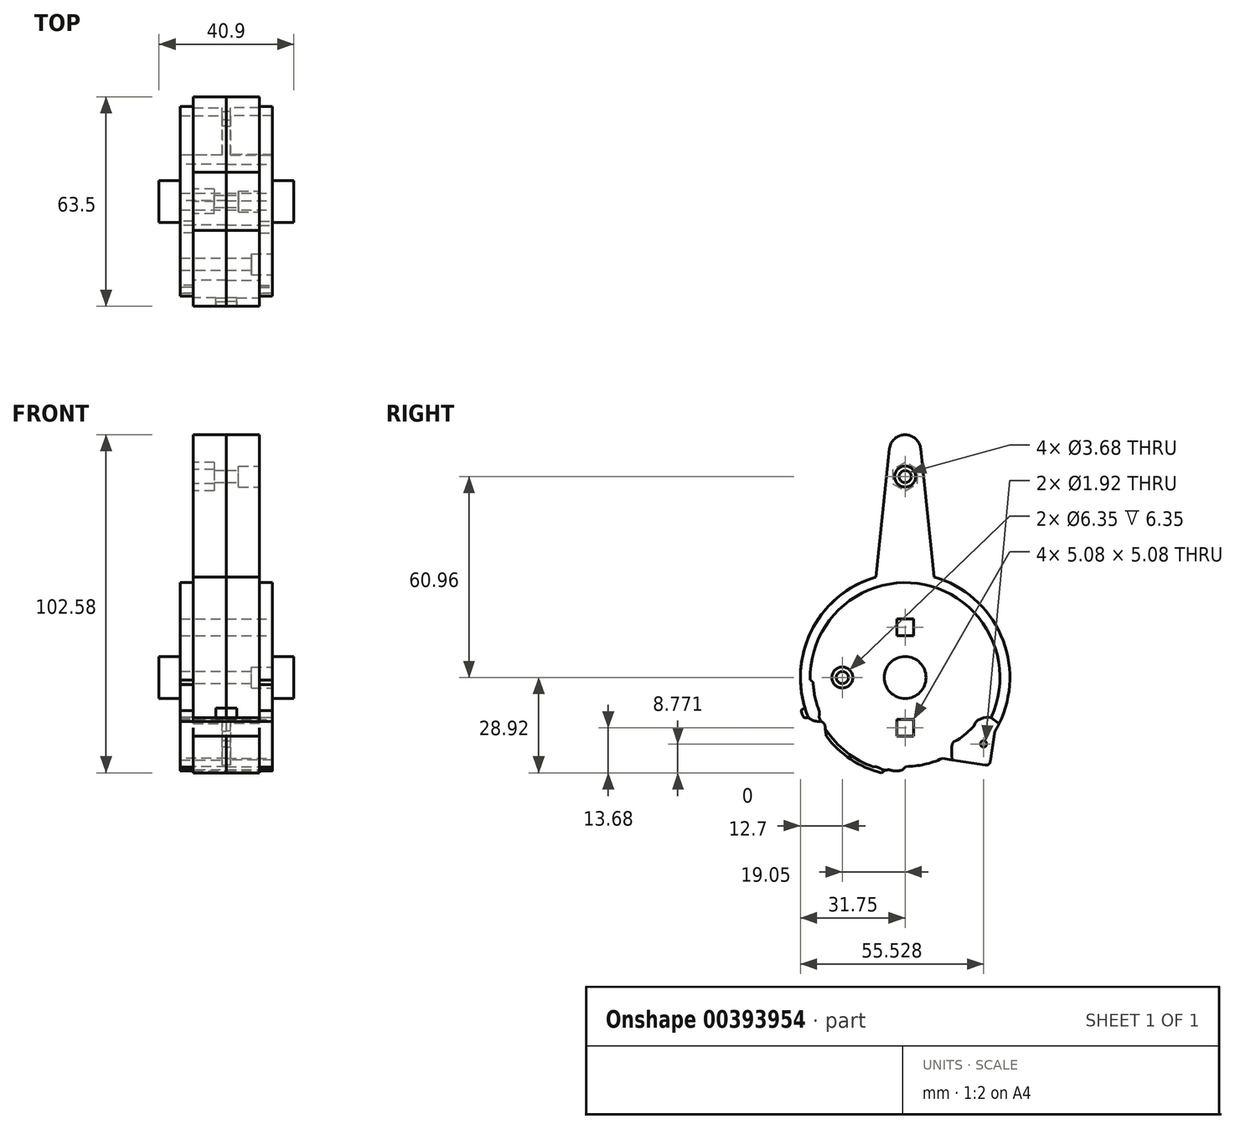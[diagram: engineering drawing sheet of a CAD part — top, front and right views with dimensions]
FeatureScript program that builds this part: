
annotation { "Feature Type Name" : "Feature", "Feature Type Description" : "" }
export const myFeature = defineFeature(function(context is Context, id is Id, definition is map)
    precondition{}
    {
        {
            var Q0;
            Q0=qCreatedBy(makeId("Right.planeOp"),FACE);
            var sketch = newSketch(context, id + "F0", { "sketchPlane" : qUnion([Q0])});
            skArc(sketch, "E0", {"start": v(-8.82, 30.5) * mm, "mid": v(-28.52, -13.96) * mm, "end": v(18.67, -25.68) * mm});
            skLineSegment(sketch, "E1", {"start": v(-4.74, 69.4) * mm, "end": v(-8.82, 30.5) * mm});
            skLineSegment(sketch, "E2", {"start": v(4.74, 69.4) * mm, "end": v(8.82, 30.5) * mm});
            skLineSegment(sketch, "E3", {"start": v(8.82, 30.5) * mm, "end": v(8.82, 30.5) * mm});
            skArc(sketch, "E4.filletArc", {"start": v(4.74, 69.4) * mm, "mid": v(0, 73.66) * mm, "end": v(-4.74, 69.4) * mm});
            skLineSegment(sketch, "E5", {"start": v(18.67, -25.68) * mm, "end": v(25.61, -26.77) * mm});
            skLineSegment(sketch, "E6", {"start": v(25.61, -26.77) * mm, "end": v(27.25, -16.29) * mm});
            skArc(sketch, "E7.trimOffspring", {"start": v(27.25, -16.29) * mm, "mid": v(29.54, 11.64) * mm, "end": v(8.82, 30.5) * mm});
            skSolve(sketch);
        }
        {
            var Q0;
            Q0=makeQuery(id+"F0.imprint","IMPRINT",FACE,{"disambiguationData":[TD([[makeQuery(id+"F0.imprint","IMPRINT",EDGE,{"derivedFrom":sQuery(id+"F0.wireOp",EDGE,"E0")}),1.0]])]});
            extrude(context, id + "F1", {"entities" : qUnion([Q0]), "depth" : 10.03 * mm});
        }
        {
            var Q0;
            Q0=qCreatedBy(makeId("Right.planeOp"),FACE);
            var sketch = newSketch(context, id + "F2", { "sketchPlane" : qUnion([Q0])});
            skCircle(sketch, "E8", {"center": v(0, 0) * mm, "radius": 28.77 * mm});
            skSolve(sketch);
        }
        {
            var Q0;
            Q0 = qSketchRegion(id + "F2", true);
            extrude(context, id + "F3", {"entities" : qUnion([Q0]), "operationType" : NewBodyOperationType.ADD, "depth" : 13.97 * mm});
        }
        {
            var Q0;
            Q0=qCreatedBy(makeId("Right.planeOp"),FACE);
            var sketch = newSketch(context, id + "F4", { "sketchPlane" : qUnion([Q0])});
            skCircle(sketch, "E9", {"center": v(0, 0) * mm, "radius": 6.35 * mm});
            skSolve(sketch);
        }
        {
            var Q0;
            Q0 = qSketchRegion(id + "F4", true);
            extrude(context, id + "F5", {"entities" : qUnion([Q0]), "operationType" : NewBodyOperationType.ADD, "depth" : 20.45 * mm});
        }
        {
            var Q0;
            Q0=makeQuery(id+"F3.opExtrude","CAP_FACE",FACE,{"disambiguationData":[OSD([sQuery(id+"F2.wireOp",EDGE,"E8")])],"isStart":false});
            var sketch = newSketch(context, id + "F6", { "sketchPlane" : qUnion([Q0])});
            skLineSegment(sketch, "E10.0", {"start": v(-8.82, 30.5) * mm, "end": v(-8.82, 30.5) * mm});
            skArc(sketch, "E11", {"start": v(-7.15, -28.92) * mm, "mid": v(-16.5, -24.81) * mm, "end": v(-23.9, -17.8) * mm});
            skFitSpline(sketch, "E12", {"points": [v(-7.15, -28.92) * mm, v(-6.46, -28.47) * mm, v(-6.2, -28.23) * mm, v(-5.89, -28.08) * mm, v(-5.55, -28.03) * mm, v(-5, -28) * mm, v(-4.31, -28.13) * mm, v(-3.35, -28.29) * mm, v(-2.28, -28.29) * mm, v(-1.37, -28.2) * mm, v(-0.54, -27.74) * mm, v(0.18, -27) * mm], "startDerivative": vector(7.94, 4.82) * mm, "endDerivative": vector(3.82, 6.45) * mm});
            skArc(sketch, "E13", {"start": v(0.18, -27) * mm, "mid": v(5.87, -26.35) * mm, "end": v(11.29, -24.53) * mm});
            skArc(sketch, "E14", {"start": v(-29.29, -12.26) * mm, "mid": v(-8.56, -30.57) * mm, "end": v(18.67, -25.68) * mm});
            skFitSpline(sketch, "E15", {"points": [v(-29.29, -12.26) * mm, v(-28.7, -12.62) * mm, v(-28.12, -12.97) * mm, v(-27.44, -13.17) * mm, v(-26.86, -13.25) * mm, v(-26.06, -13.36) * mm, v(-25.83, -13.34) * mm, v(-25.47, -13.37) * mm, v(-25.09, -13.51) * mm, v(-24.75, -13.83) * mm, v(-24.45, -14.2) * mm, v(-24.33, -14.51) * mm, v(-24.28, -14.82) * mm, v(-24.27, -15.1) * mm, v(-24.22, -15.52) * mm, v(-24.15, -16.14) * mm, v(-23.9, -17.8) * mm], "startDerivative": vector(8.22, -5.06) * mm, "endDerivative": vector(3.58, -22.61) * mm});
            skLineSegment(sketch, "E16.0", {"start": v(11.29, -24.53) * mm, "end": v(18.67, -25.68) * mm});
            skPoint(sketch, "E17.orphan", {"position": v(18.67, -25.68) * mm});
            skPoint(sketch, "E18.orphan", {"position": v(25.61, -26.77) * mm});
            skSolve(sketch);
        }
        {
            var Q0;
            Q0 = qSketchRegion(id + "F6", true);
            extrude(context, id + "F7", {"entities" : qUnion([Q0]), "operationType" : NewBodyOperationType.REMOVE, "endBound" : BoundingType.THROUGH_ALL, "oppositeDirection" : true, "depth" : 25.4 * mm});
        }
        {
            var Q0;
            Q0=qCreatedBy(makeId("Right.planeOp"),FACE);
            var sketch = newSketch(context, id + "F8", { "sketchPlane" : qUnion([Q0])});
            skFitSpline(sketch, "E19", {"points": [v(-29.98, -9.37) * mm, v(-30.97, -9.54) * mm, v(-31.46, -9.91) * mm, v(-31.42, -10.4) * mm, v(-31.3, -11) * mm, v(-31.05, -11.53) * mm, v(-30.78, -12.05) * mm, v(-30.13, -12.26) * mm, v(-29.34, -12.26) * mm, v(-29.1, -12.19) * mm, v(-29.98, -9.37) * mm]});
            skSolve(sketch);
        }
        {
            var Q0;
            Q0 = qSketchRegion(id + "F8", true);
            extrude(context, id + "F9", {"entities" : qUnion([Q0]), "operationType" : NewBodyOperationType.ADD, "depth" : 3.17 * mm});
        }
        {
            var Q0;
            Q0=qCreatedBy(makeId("Right.planeOp"),FACE);
            cPlane(context, id + "F10", {"entities" : qUnion([Q0]), "cplaneType" : CPlaneType.OFFSET, "offset" : 1.27 * mm, "width" : 152.4 * mm, "height" : 152.4 * mm});
        }
        {
            var Q0;
            Q0=qCreatedBy(id+"F10.planeOp",FACE);
            var sketch = newSketch(context, id + "F11", { "sketchPlane" : qUnion([Q0])});
            skPoint(sketch, "E20.0", {"position": v(19.93, -25.88) * mm});
            skLineSegment(sketch, "E21.0", {"start": v(25.61, -26.77) * mm, "end": v(27.25, -16.29) * mm});
            skArc(sketch, "E22.0", {"start": v(27.25, -16.29) * mm, "mid": v(27.89, -15.17) * mm, "end": v(28.48, -14.03) * mm});
            skLineSegment(sketch, "E23", {"start": v(26.08, -12.14) * mm, "end": v(28.48, -14.03) * mm});
            skPoint(sketch, "E24.orphan", {"position": v(-25.47, -13.37) * mm});
            skPoint(sketch, "E25.orphan", {"position": v(8.82, 30.5) * mm});
            skLineSegment(sketch, "E26", {"start": v(14.25, -24.99) * mm, "end": v(25.61, -26.77) * mm});
            skFitSpline(sketch, "E27", {"points": [v(26.08, -12.14) * mm, v(24.03, -12.14) * mm, v(21.51, -13.45) * mm, v(20.75, -14.85) * mm, v(19.28, -16.22) * mm, v(17.23, -18.05) * mm, v(15.6, -19.12) * mm, v(14.47, -19.84) * mm, v(14.25, -24.99) * mm], "startDerivative": vector(-16.47, 2.03) * mm, "endDerivative": vector(2.36, -34.88) * mm});
            skSolve(sketch);
        }
        {
            var Q0;
            Q0 = qSketchRegion(id + "F11", true);
            extrude(context, id + "F12", {"entities" : qUnion([Q0]), "operationType" : NewBodyOperationType.REMOVE, "endBound" : BoundingType.THROUGH_ALL, "depth" : 25.4 * mm});
        }
        {
            var Q0;
            Q0=makeQuery(id+"F12.boolean.opBoolean","COPY",FACE,{"derivedFrom":makeQuery(id+"F12.opExtrude","CAP_FACE",FACE,{"disambiguationData":[OSD([sQuery(id+"F11.wireOp",EDGE,"8e69ba01-a64c-4ecc-a6ff-eef0bb5ade50.0"),sQuery(id+"F11.wireOp",EDGE,"E21.0"),sQuery(id+"F11.wireOp",EDGE,"E22.0"),sQuery(id+"F11.wireOp",EDGE,"E23"),sQuery(id+"F11.wireOp",EDGE,"E26")])],"isStart":true})});
            var sketch = newSketch(context, id + "F13", { "sketchPlane" : qUnion([Q0])});
            skCircle(sketch, "E28", {"center": v(23.78, -20.15) * mm, "radius": 0.96 * mm});
            skSolve(sketch);
        }
        {
            var Q0;
            Q0 = qSketchRegion(id + "F13", true);
            extrude(context, id + "F14", {"entities" : qUnion([Q0]), "operationType" : NewBodyOperationType.REMOVE, "endBound" : BoundingType.THROUGH_ALL, "oppositeDirection" : true, "depth" : 25.4 * mm});
        }
        {
            var Q0;
            {var subQ0=makeQuery(id+"F1.opExtrude","SWEPT_EDGE",EDGE,{"disambiguationData":[OSD([sQuery(id+"F0.wireOp",EDGE,"E5"),sQuery(id+"F0.wireOp",EDGE,"E6")])]});Q0=makeQuery(id+"F25jmTreoOPRgd2_1.boolean.opBoolean","MERGE",EDGE,{"derivedFrom":[subQ0,makeQuery(id+"F25jmTreoOPRgd2_1.opPattern","COPY",EDGE,{"derivedFrom":subQ0,"instanceName":"1"})]});}
            fillet(context, id + "F15", {"entities" : qUnion([Q0]), "radius" : 1.27 * mm, "tangentPropagation" : true, "allowEdgeOverflow" : false});
        }
        {
            var Q0;
            Q0=makeQuery(id+"F5.opExtrude","CAP_FACE",FACE,{"disambiguationData":[OSD([sQuery(id+"F4.wireOp",EDGE,"E9")])],"isStart":false});
            var sketch = newSketch(context, id + "F16", { "sketchPlane" : qUnion([Q0])});
            skCircle(sketch, "E29", {"center": v(0, 0) * mm, "radius": 3.18 * mm});
            skSolve(sketch);
        }
        {
            var Q0;
            Q0=makeQuery(id+"F3.opExtrude","CAP_FACE",FACE,{"disambiguationData":[OSD([sQuery(id+"F2.wireOp",EDGE,"E8")])],"isStart":false});
            var sketch = newSketch(context, id + "F17", { "sketchPlane" : qUnion([Q0])});
            skArc(sketch, "E30", {"start": v(-28.76, -0.75) * mm, "mid": v(-28.02, -6.52) * mm, "end": v(-26.13, -12.03) * mm});
            skFitSpline(sketch, "E31", {"points": [v(-28.76, -0.75) * mm, v(-27.98, -1.46) * mm, v(-27.86, -2.22) * mm], "startDerivative": vector(1.75, -1.24) * mm, "endDerivative": vector(-0.01, -1.72) * mm});
            skArc(sketch, "E32", {"start": v(-27.86, -2.22) * mm, "mid": v(-27.26, -6.2) * mm, "end": v(-26.08, -10.05) * mm});
            skFitSpline(sketch, "E33", {"points": [v(-26.08, -10.05) * mm, v(-26, -10.4) * mm, v(-25.98, -10.96) * mm, v(-26.13, -12.03) * mm], "startDerivative": vector(0.35, -1.3) * mm, "endDerivative": vector(-0.44, -2.63) * mm});
            skSolve(sketch);
        }
        {
            var Q0;
            Q0 = qSketchRegion(id + "F17", true);
            var Q1;
            {var subQ0=sQuery(id+"F0.wireOp",EDGE,"E2");var subQ1=sQuery(id+"F0.wireOp",EDGE,"E1");var subQ2=sQuery(id+"F0.wireOp",EDGE,"E4.filletArc");var subQ3=sQuery(id+"F0.wireOp",EDGE,"E0");var subQ4=sQuery(id+"F0.wireOp",EDGE,"E5");var subQ5=sQuery(id+"F0.wireOp",EDGE,"E6");var subQ6=sQuery(id+"F0.wireOp",EDGE,"E7.trimOffspring");Q1=makeQuery(id+"F7.boolean.opBoolean","SPLIT",FACE,{"disambiguationData":[TD([makeQuery(id+"F1.opExtrude","SWEPT_FACE",FACE,{"disambiguationData":[OSD([subQ3])]})])],"derivedFrom":makeQuery(id+"F1.opExtrude","CAP_FACE",FACE,{"disambiguationData":[OSD([subQ3,subQ1,subQ0,subQ2,subQ4,subQ5,subQ6])],"isStart":false})});}
            extrude(context, id + "F18", {"entities" : qUnion([Q0]), "operationType" : NewBodyOperationType.REMOVE, "endBound" : BoundingType.UP_TO_SURFACE, "oppositeDirection" : true, "endBoundEntityFace" : qUnion([Q1]), "depth" : 25.4 * mm});
        }
        {
            var Q0;
            Q0=makeQuery(id+"F18.boolean.opBoolean","COPY",EDGE,{"derivedFrom":makeQuery(id+"F18.opExtrude","SWEPT_EDGE",EDGE,{"disambiguationData":[OSD([sQuery(id+"F2.wireOp",EDGE,"E8"),sQuery(id+"F17.wireOp",EDGE,"E30"),sQuery(id+"F17.wireOp",EDGE,"E33")])]})});
            var Q1;
            Q1=makeQuery(id+"F7.boolean.opBoolean","INTERSECT",EDGE,{"disambiguationData":[OD(0.0)],"derivedFrom":[makeQuery(id+"F3.opExtrude","SWEPT_FACE",FACE,{"disambiguationData":[OSD([sQuery(id+"F2.wireOp",EDGE,"E8")])]}),makeQuery(id+"F7.opExtrude","SWEPT_FACE",FACE,{"disambiguationData":[OSD([sQuery(id+"F6.wireOp",EDGE,"E15")])]})]});
            fillet(context, id + "F19", {"entities" : qUnion([Q0, Q1]), "radius" : 1.27 * mm, "tangentPropagation" : true, "allowEdgeOverflow" : false});
        }
        {
            var Q0;
            Q0=makeQuery(id+"F3.opExtrude","CAP_FACE",FACE,{"disambiguationData":[OSD([sQuery(id+"F2.wireOp",EDGE,"E8")])],"isStart":false});
            var sketch = newSketch(context, id + "F20", { "sketchPlane" : qUnion([Q0])});
            skArc(sketch, "E34", {"start": v(-25.5, -17.61) * mm, "mid": v(-17.23, -25.76) * mm, "end": v(-6.54, -30.3) * mm, "construction": true});
            skCircle(sketch, "E35", {"center": v(-9.06, -29.63) * mm, "radius": 2.54 * mm});
            skLineSegment(sketch, "E36", {"start": v(-9.06, -29.63) * mm, "end": v(0, 0) * mm, "construction": true});
            skSolve(sketch);
        }
        {
            var Q0;
            Q0 = qSketchRegion(id + "F20", true);
            var Q1;
            Q1=makeQuery(id+"F7.boolean.opBoolean","SPLIT",FACE,{"disambiguationData":[TD([makeQuery(id+"F7.opExtrude","SWEPT_FACE",FACE,{"disambiguationData":[OSD([sQuery(id+"F6.wireOp",EDGE,"E11")])]})])],"derivedFrom":makeQuery(id+"F1.opExtrude","CAP_FACE",FACE,{"disambiguationData":[OSD([sQuery(id+"F0.wireOp",EDGE,"E0"),sQuery(id+"F0.wireOp",EDGE,"E1"),sQuery(id+"F0.wireOp",EDGE,"E2"),sQuery(id+"F0.wireOp",EDGE,"E4.filletArc"),sQuery(id+"F0.wireOp",EDGE,"E5"),sQuery(id+"F0.wireOp",EDGE,"E6"),sQuery(id+"F0.wireOp",EDGE,"E7.trimOffspring")])],"isStart":false})});
            extrude(context, id + "F21", {"entities" : qUnion([Q0]), "operationType" : NewBodyOperationType.REMOVE, "endBound" : BoundingType.UP_TO_SURFACE, "oppositeDirection" : true, "endBoundEntityFace" : qUnion([Q1]), "depth" : 25.4 * mm});
        }
        {
            var Q0;
            Q0=makeQuery(id+"F1.opExtrude","SWEPT_BODY",BODY,{"disambiguationData":[OSD([sQuery(id+"F0.wireOp",EDGE,"E0"),sQuery(id+"F0.wireOp",EDGE,"E1"),sQuery(id+"F0.wireOp",EDGE,"E2"),sQuery(id+"F0.wireOp",EDGE,"E4.filletArc"),sQuery(id+"F0.wireOp",EDGE,"E5"),sQuery(id+"F0.wireOp",EDGE,"E6"),sQuery(id+"F0.wireOp",EDGE,"E7.trimOffspring")])]});
            var Q1;
            Q1=qCreatedBy(makeId("Right.planeOp"),FACE);
            mirror(context, id + "F22", {"entities" : qUnion([Q0]), "mirrorPlane" : qUnion([Q1])});
        }
        {
            var Q0;
            Q0=qCreatedBy(makeId("Right.planeOp"),FACE);
            var sketch = newSketch(context, id + "F23", { "sketchPlane" : qUnion([Q0])});
            skLineSegment(sketch, "E37.bottom", {"start": v(-2.54, 17.78) * mm, "end": v(2.54, 17.78) * mm});
            skLineSegment(sketch, "E37.top", {"start": v(-2.54, 12.7) * mm, "end": v(2.54, 12.7) * mm});
            skLineSegment(sketch, "E37.left", {"start": v(-2.54, 17.78) * mm, "end": v(-2.54, 12.7) * mm});
            skLineSegment(sketch, "E37.right", {"start": v(2.54, 17.78) * mm, "end": v(2.54, 12.7) * mm});
            skLineSegment(sketch, "E38.bottom", {"start": v(-2.54, -12.7) * mm, "end": v(2.54, -12.7) * mm});
            skLineSegment(sketch, "E38.top", {"start": v(-2.54, -17.78) * mm, "end": v(2.54, -17.78) * mm});
            skLineSegment(sketch, "E38.left", {"start": v(-2.54, -12.7) * mm, "end": v(-2.54, -17.78) * mm});
            skLineSegment(sketch, "E38.right", {"start": v(2.54, -12.7) * mm, "end": v(2.54, -17.78) * mm});
            skSolve(sketch);
        }
        {
            var Q0;
            Q0 = qSketchRegion(id + "F23", true);
            extrude(context, id + "F24", {"entities" : qUnion([Q0]), "operationType" : NewBodyOperationType.REMOVE, "endBound" : BoundingType.THROUGH_ALL, "oppositeDirection" : true, "depth" : 10.16 * mm, "hasSecondDirection" : true, "secondDirectionBound" : SecondDirectionBoundingType.THROUGH_ALL, "secondDirectionOppositeDirection" : false, "secondDirectionDepth" : 10.16 * mm});
        }
        {
            var Q0;
            Q0=makeQuery(id+"F3.opExtrude","CAP_FACE",FACE,{"disambiguationData":[OSD([sQuery(id+"F2.wireOp",EDGE,"E8")])],"isStart":false});
            var sketch = newSketch(context, id + "F25", { "sketchPlane" : qUnion([Q0])});
            skCircle(sketch, "E39", {"center": v(-19.05, 0) * mm, "radius": 2.85 * mm});
            skSolve(sketch);
        }
        {
            var Q0;
            Q0=sQuery(id+"F25.wireOp",VERTEX,"E39.center");
            var Q1;
            Q1=makeQuery(id+"F1.opExtrude","SWEPT_BODY",BODY,{"disambiguationData":[OSD([sQuery(id+"F0.wireOp",EDGE,"E0"),sQuery(id+"F0.wireOp",EDGE,"E1"),sQuery(id+"F0.wireOp",EDGE,"E2"),sQuery(id+"F0.wireOp",EDGE,"E4.filletArc"),sQuery(id+"F0.wireOp",EDGE,"E5"),sQuery(id+"F0.wireOp",EDGE,"E6"),sQuery(id+"F0.wireOp",EDGE,"E7.trimOffspring")])]});
            var Q2;
            Q2=makeQuery(id+"F22.opPattern","COPY",BODY,{"derivedFrom":makeQuery(id+"F1.opExtrude","SWEPT_BODY",BODY,{"disambiguationData":[OSD([sQuery(id+"F0.wireOp",EDGE,"E0"),sQuery(id+"F0.wireOp",EDGE,"E1"),sQuery(id+"F0.wireOp",EDGE,"E2"),sQuery(id+"F0.wireOp",EDGE,"E4.filletArc"),sQuery(id+"F0.wireOp",EDGE,"E5"),sQuery(id+"F0.wireOp",EDGE,"E6"),sQuery(id+"F0.wireOp",EDGE,"E7.trimOffspring")])]}),"instanceName":"1"});
            hole(context, id + "F26", {"style" : HoleStyle.C_BORE, "endStyle" : HoleEndStyle.THROUGH, "holeDiameter" : 3.68 * mm, "cBoreDiameter" : 6.35 * mm, "cBoreDepth" : 6.35 * mm, "isTappedThrough" : true, "tappedDepth" : 12.7 * mm, "tapClearance" : 3, "startFromSketch" : true, "locations" : qUnion([Q0]), "scope" : qUnion([Q1, Q2])});
        }
        {
            var Q0;
            {var subQ0=sQuery(id+"F0.wireOp",EDGE,"E2");var subQ1=sQuery(id+"F0.wireOp",EDGE,"E1");var subQ2=sQuery(id+"F0.wireOp",EDGE,"E4.filletArc");var subQ3=sQuery(id+"F0.wireOp",EDGE,"E0");var subQ4=sQuery(id+"F0.wireOp",EDGE,"E5");var subQ5=sQuery(id+"F0.wireOp",EDGE,"E6");var subQ6=sQuery(id+"F0.wireOp",EDGE,"E7.trimOffspring");Q0=makeQuery(id+"F18.boolean.opBoolean","MERGE",FACE,{"derivedFrom":[makeQuery(id+"F7.boolean.opBoolean","SPLIT",FACE,{"disambiguationData":[TD([makeQuery(id+"F1.opExtrude","SWEPT_FACE",FACE,{"disambiguationData":[OSD([subQ3])]})])],"derivedFrom":makeQuery(id+"F1.opExtrude","CAP_FACE",FACE,{"disambiguationData":[OSD([subQ3,subQ1,subQ0,subQ2,subQ4,subQ5,subQ6])],"isStart":false})}),makeQuery(id+"F18.opExtrude","CAP_FACE",FACE,{"disambiguationData":[OSD([sQuery(id+"F17.wireOp",EDGE,"E30"),sQuery(id+"F17.wireOp",EDGE,"E31"),sQuery(id+"F17.wireOp",EDGE,"E32"),sQuery(id+"F17.wireOp",EDGE,"E33")])],"isStart":false})]});}
            var sketch = newSketch(context, id + "F27", { "sketchPlane" : qUnion([Q0])});
            skPoint(sketch, "E40", {"position": v(0, 60.96) * mm});
            skSolve(sketch);
        }
        {
            var Q0;
            Q0=sQuery(id+"F27.wireOp",VERTEX,"E40");
            var Q1;
            Q1=makeQuery(id+"F1.opExtrude","SWEPT_BODY",BODY,{"disambiguationData":[OSD([sQuery(id+"F0.wireOp",EDGE,"E0"),sQuery(id+"F0.wireOp",EDGE,"E1"),sQuery(id+"F0.wireOp",EDGE,"E2"),sQuery(id+"F0.wireOp",EDGE,"E4.filletArc"),sQuery(id+"F0.wireOp",EDGE,"E5"),sQuery(id+"F0.wireOp",EDGE,"E6"),sQuery(id+"F0.wireOp",EDGE,"E7.trimOffspring")])]});
            var Q2;
            Q2=makeQuery(id+"F22.opPattern","COPY",BODY,{"derivedFrom":makeQuery(id+"F1.opExtrude","SWEPT_BODY",BODY,{"disambiguationData":[OSD([sQuery(id+"F0.wireOp",EDGE,"E0"),sQuery(id+"F0.wireOp",EDGE,"E1"),sQuery(id+"F0.wireOp",EDGE,"E2"),sQuery(id+"F0.wireOp",EDGE,"E4.filletArc"),sQuery(id+"F0.wireOp",EDGE,"E5"),sQuery(id+"F0.wireOp",EDGE,"E6"),sQuery(id+"F0.wireOp",EDGE,"E7.trimOffspring")])]}),"instanceName":"1"});
            hole(context, id + "F28", {"style" : HoleStyle.C_BORE, "endStyle" : HoleEndStyle.THROUGH, "holeDiameter" : 3.68 * mm, "cBoreDiameter" : 6.35 * mm, "cBoreDepth" : 6.35 * mm, "isTappedThrough" : true, "tappedDepth" : 12.7 * mm, "tapClearance" : 3, "startFromSketch" : true, "locations" : qUnion([Q0]), "scope" : qUnion([Q1, Q2])});
        }
        {
            var Q0;
            {var subQ0=sQuery(id+"F0.wireOp",EDGE,"E2");var subQ1=sQuery(id+"F0.wireOp",EDGE,"E1");var subQ2=sQuery(id+"F0.wireOp",EDGE,"E4.filletArc");var subQ3=sQuery(id+"F0.wireOp",EDGE,"E0");var subQ4=sQuery(id+"F0.wireOp",EDGE,"E5");var subQ5=sQuery(id+"F0.wireOp",EDGE,"E6");var subQ6=sQuery(id+"F0.wireOp",EDGE,"E7.trimOffspring");Q0=makeQuery(id+"F22.opPattern","COPY",FACE,{"derivedFrom":makeQuery(id+"F18.boolean.opBoolean","MERGE",FACE,{"derivedFrom":[makeQuery(id+"F7.boolean.opBoolean","SPLIT",FACE,{"disambiguationData":[TD([makeQuery(id+"F1.opExtrude","SWEPT_FACE",FACE,{"disambiguationData":[OSD([subQ3])]})])],"derivedFrom":makeQuery(id+"F1.opExtrude","CAP_FACE",FACE,{"disambiguationData":[OSD([subQ3,subQ1,subQ0,subQ2,subQ4,subQ5,subQ6])],"isStart":false})}),makeQuery(id+"F18.opExtrude","CAP_FACE",FACE,{"disambiguationData":[OSD([sQuery(id+"F17.wireOp",EDGE,"E30"),sQuery(id+"F17.wireOp",EDGE,"E31"),sQuery(id+"F17.wireOp",EDGE,"E32"),sQuery(id+"F17.wireOp",EDGE,"E33")])],"isStart":false})]}),"instanceName":"1"});}
            var sketch = newSketch(context, id + "F29", { "sketchPlane" : qUnion([Q0])});
            skCircle(sketch, "E41.cCircle", {"center": v(0, 60.96) * mm, "radius": 4.3 * mm, "construction": true});
            skLineSegment(sketch, "E41.0", {"start": v(3.73, 58.8) * mm, "end": v(0, 56.65) * mm});
            skLineSegment(sketch, "E41.1", {"start": v(0, 56.65) * mm, "end": v(-3.73, 58.8) * mm});
            skLineSegment(sketch, "E41.2", {"start": v(-3.73, 58.8) * mm, "end": v(-3.73, 63.11) * mm});
            skLineSegment(sketch, "E41.3", {"start": v(-3.73, 63.11) * mm, "end": v(0, 65.27) * mm});
            skLineSegment(sketch, "E41.4", {"start": v(0, 65.27) * mm, "end": v(3.73, 63.11) * mm});
            skLineSegment(sketch, "E41.5", {"start": v(3.73, 63.11) * mm, "end": v(3.73, 58.8) * mm});
            skSolve(sketch);
        }
        {
            var Q0;
            Q0=makeQuery(id+"F29.imprint","IMPRINT",FACE,{"disambiguationData":[TD([[makeQuery(id+"F29.imprint","IMPRINT",EDGE,{"derivedFrom":sQuery(id+"F29.wireOp",EDGE,"E41.0")}),-1.0]])]});
            extrude(context, id + "F30", {"entities" : qUnion([Q0]), "operationType" : NewBodyOperationType.REMOVE, "oppositeDirection" : true, "depth" : 6.35 * mm});
        }
    });
